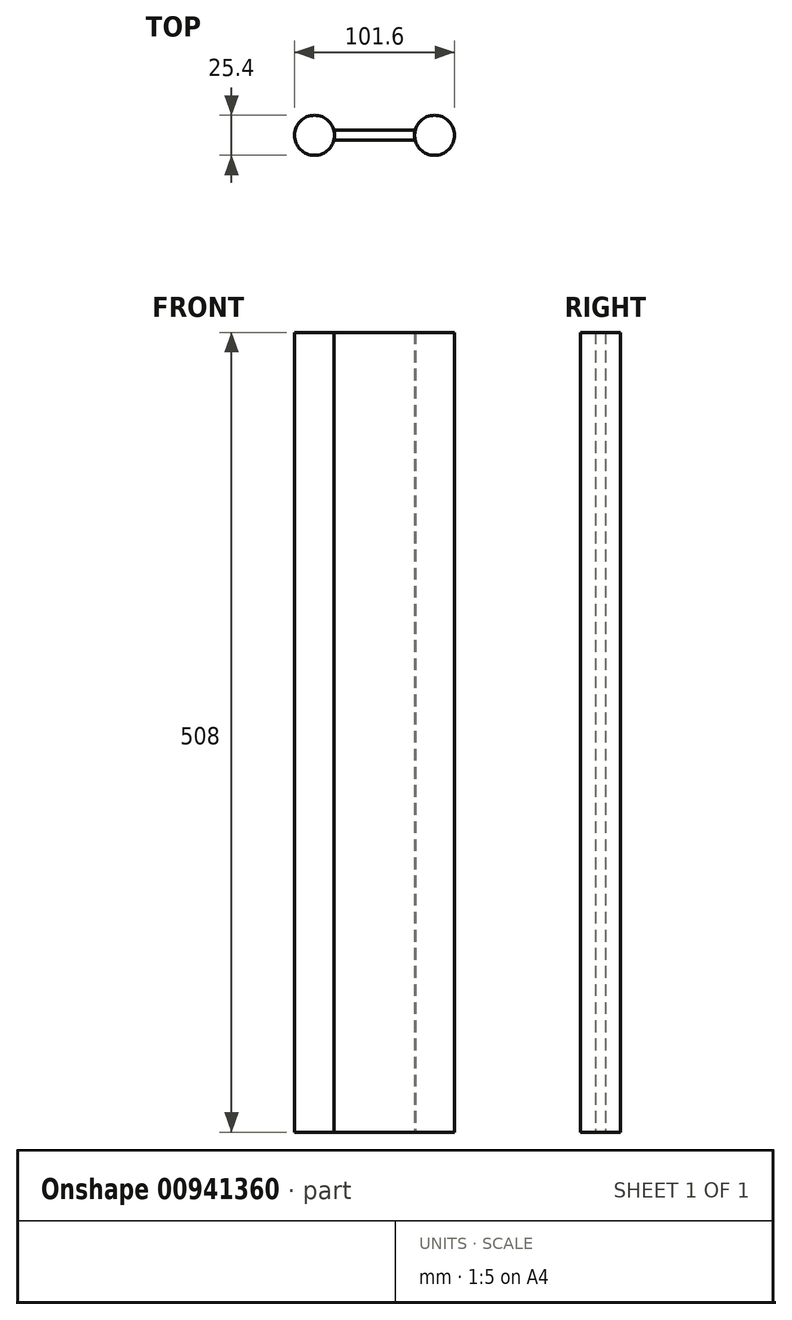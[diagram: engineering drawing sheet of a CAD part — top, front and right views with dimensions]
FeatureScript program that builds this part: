
annotation { "Feature Type Name" : "Feature", "Feature Type Description" : "" }
export const myFeature = defineFeature(function(context is Context, id is Id, definition is map)
    precondition{}
    {
        {
            var Q0;
            Q0=qCreatedBy(makeId("Top.planeOp"),FACE);
            var sketch = newSketch(context, id + "F0", { "sketchPlane" : qUnion([Q0])});
            skCircle(sketch, "E0", {"center": v(-38.1, 0) * mm, "radius": 12.7 * mm});
            skCircle(sketch, "E1", {"center": v(38.1, 0) * mm, "radius": 12.7 * mm});
            skSolve(sketch);
        }
        {
            var Q0;
            Q0=qCreatedBy(makeId("Top.planeOp"),FACE);
            var sketch = newSketch(context, id + "F1", { "sketchPlane" : qUnion([Q0])});
            skLineSegment(sketch, "E2.bottom", {"start": v(-25.74, -3.18) * mm, "end": v(25.94, -3.18) * mm});
            skLineSegment(sketch, "E2.top", {"start": v(-25.74, 3.18) * mm, "end": v(25.94, 3.18) * mm});
            skArc(sketch, "E3", {"start": v(-25.74, -3.17) * mm, "mid": v(-25.45, 0) * mm, "end": v(-25.74, 3.17) * mm});
            skArc(sketch, "E4", {"start": v(25.94, 3.18) * mm, "mid": v(25.52, 0) * mm, "end": v(25.94, -3.18) * mm});
            skSolve(sketch);
        }
        {
            var Q0;
            Q0 = qSketchRegion(id + "F0", true);
            var Q1;
            Q1=makeQuery(id+"F1.imprint","IMPRINT",FACE,{"disambiguationData":[TD([[makeQuery(id+"F1.imprint","IMPRINT",EDGE,{"derivedFrom":sQuery(id+"F1.wireOp",EDGE,"E2.bottom")}),1.0]])]});
            extrude(context, id + "F2", {"entities" : qUnion([Q0, Q1]), "depth" : 508 * mm, "offsetDistance" : 25.4 * mm});
        }
    });
